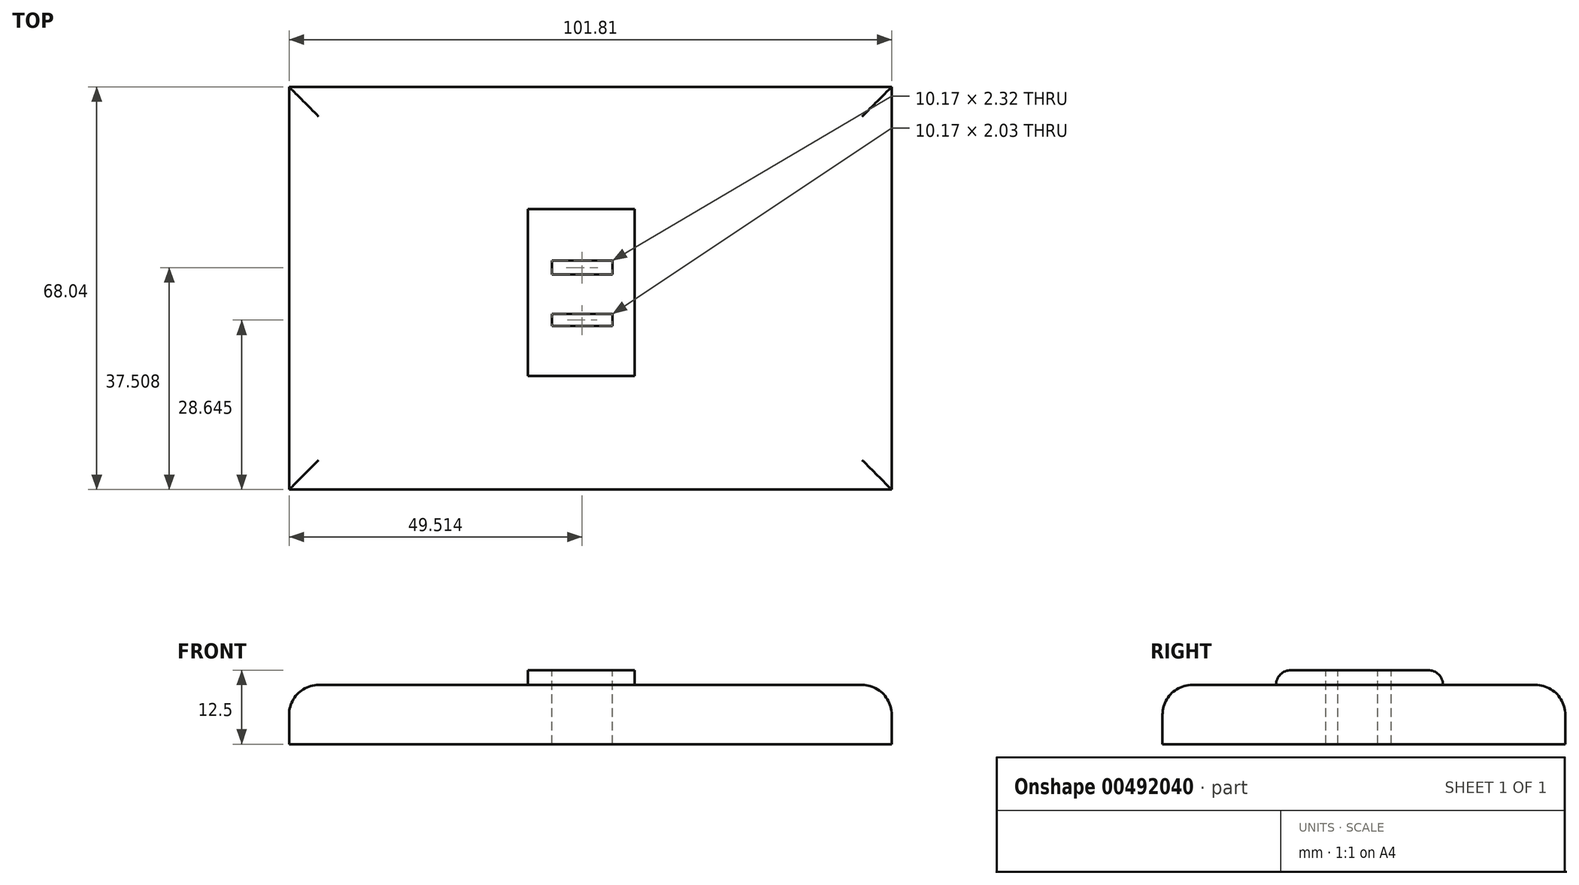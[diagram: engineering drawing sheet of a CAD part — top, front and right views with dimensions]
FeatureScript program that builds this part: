
annotation { "Feature Type Name" : "Feature", "Feature Type Description" : "" }
export const myFeature = defineFeature(function(context is Context, id is Id, definition is map)
    precondition{}
    {
        {
            var Q0;
            Q0=qCreatedBy(makeId("Top.planeOp"),FACE);
            var sketch = newSketch(context, id + "F0", { "sketchPlane" : qUnion([Q0])});
            skLineSegment(sketch, "E0.bottom", {"start": v(-49.95, 29.37) * mm, "end": v(51.86, 29.37) * mm});
            skLineSegment(sketch, "E0.top", {"start": v(-49.95, -38.67) * mm, "end": v(51.86, -38.67) * mm});
            skLineSegment(sketch, "E0.left", {"start": v(-49.95, 29.37) * mm, "end": v(-49.95, -38.67) * mm});
            skLineSegment(sketch, "E0.right", {"start": v(51.86, 29.37) * mm, "end": v(51.86, -38.67) * mm});
            skSolve(sketch);
        }
        {
            var Q0;
            Q0=qSketchRegion(id+"F0",true);
            extrude(context, id + "F1", {"entities" : qUnion([Q0]), "depth" : 10 * mm});
        }
        {
            var Q0;
            Q0=makeQuery(id+"F1.opExtrude","CAP_EDGE",EDGE,{"disambiguationData":[OSD([sQuery(id+"F0.wireOp",EDGE,"E0.left")])],"isStart":false});
            var Q1;
            Q1=makeQuery(id+"F1.opExtrude","CAP_FACE",FACE,{"disambiguationData":[OSD([sQuery(id+"F0.wireOp",EDGE,"E0.bottom"),sQuery(id+"F0.wireOp",EDGE,"E0.top"),sQuery(id+"F0.wireOp",EDGE,"E0.left"),sQuery(id+"F0.wireOp",EDGE,"E0.right")])],"isStart":false});
            fillet(context, id + "F2", {"entities" : qUnion([Q0, Q1]), "radius" : 5 * mm, "tangentPropagation" : true, "allowEdgeOverflow" : false});
        }
        {
            var Q0;
            Q0=makeQuery(id+"F1.opExtrude","CAP_FACE",FACE,{"disambiguationData":[OSD([sQuery(id+"F0.wireOp",EDGE,"E0.bottom"),sQuery(id+"F0.wireOp",EDGE,"E0.top"),sQuery(id+"F0.wireOp",EDGE,"E0.left"),sQuery(id+"F0.wireOp",EDGE,"E0.right")])],"isStart":false});
            var sketch = newSketch(context, id + "F3", { "sketchPlane" : qUnion([Q0])});
            skLineSegment(sketch, "E1.bottom", {"start": v(-9.59, 8.72) * mm, "end": v(8.43, 8.72) * mm});
            skLineSegment(sketch, "E1.top", {"start": v(-9.59, -19.47) * mm, "end": v(8.43, -19.47) * mm});
            skLineSegment(sketch, "E1.left", {"start": v(-9.59, 8.72) * mm, "end": v(-9.59, -19.47) * mm});
            skLineSegment(sketch, "E1.right", {"start": v(8.43, 8.72) * mm, "end": v(8.43, -19.47) * mm});
            skSolve(sketch);
        }
        {
            var Q0;
            Q0 = qSketchRegion(id + "F3", true);
            extrude(context, id + "F4", {"entities" : qUnion([Q0]), "operationType" : NewBodyOperationType.ADD, "depth" : 2.5 * mm});
        }
        {
            var Q0;
            Q0=makeQuery(id+"F4.opExtrude","CAP_FACE",FACE,{"disambiguationData":[OSD([sQuery(id+"F3.wireOp",EDGE,"E1.bottom"),sQuery(id+"F3.wireOp",EDGE,"E1.top"),sQuery(id+"F3.wireOp",EDGE,"E1.left"),sQuery(id+"F3.wireOp",EDGE,"E1.right")])],"isStart":false});
            var sketch = newSketch(context, id + "F5", { "sketchPlane" : qUnion([Q0])});
            skLineSegment(sketch, "E2.bottom", {"start": v(-5.52, 0) * mm, "end": v(4.65, 0) * mm});
            skLineSegment(sketch, "E2.top", {"start": v(-5.52, -2.32) * mm, "end": v(4.65, -2.32) * mm});
            skLineSegment(sketch, "E2.left", {"start": v(-5.52, 0) * mm, "end": v(-5.52, -2.32) * mm});
            skLineSegment(sketch, "E2.right", {"start": v(4.65, 0) * mm, "end": v(4.65, -2.32) * mm});
            skLineSegment(sketch, "E3.bottom", {"start": v(-5.52, -9) * mm, "end": v(4.65, -9) * mm});
            skLineSegment(sketch, "E3.top", {"start": v(-5.52, -11.04) * mm, "end": v(4.65, -11.04) * mm});
            skLineSegment(sketch, "E3.left", {"start": v(-5.52, -9) * mm, "end": v(-5.52, -11.04) * mm});
            skLineSegment(sketch, "E3.right", {"start": v(4.65, -9) * mm, "end": v(4.65, -11.04) * mm});
            skSolve(sketch);
        }
        {
            var Q0;
            Q0=makeQuery(id+"F5.imprint","IMPRINT",FACE,{"disambiguationData":[TD([[makeQuery(id+"F5.imprint","IMPRINT",EDGE,{"derivedFrom":sQuery(id+"F5.wireOp",EDGE,"E3.bottom")}),-1.0]])]});
            var Q1;
            Q1=makeQuery(id+"F5.imprint","IMPRINT",FACE,{"disambiguationData":[TD([[makeQuery(id+"F5.imprint","IMPRINT",EDGE,{"derivedFrom":sQuery(id+"F5.wireOp",EDGE,"E2.bottom")}),-1.0]])]});
            extrude(context, id + "F6", {"entities" : qUnion([Q0, Q1]), "operationType" : NewBodyOperationType.REMOVE, "oppositeDirection" : true, "depth" : 25 * mm});
        }
        {
            var Q0;
            Q0=makeQuery(id+"F4.opExtrude","CAP_EDGE",EDGE,{"disambiguationData":[OSD([sQuery(id+"F3.wireOp",EDGE,"E1.top")])],"isStart":false});
            var Q1;
            Q1=makeQuery(id+"F4.opExtrude","CAP_EDGE",EDGE,{"disambiguationData":[OSD([sQuery(id+"F3.wireOp",EDGE,"E1.bottom")])],"isStart":false});
            fillet(context, id + "F7", {"entities" : qUnion([Q0, Q1]), "radius" : 2.5 * mm, "tangentPropagation" : true, "allowEdgeOverflow" : false});
        }
    });
